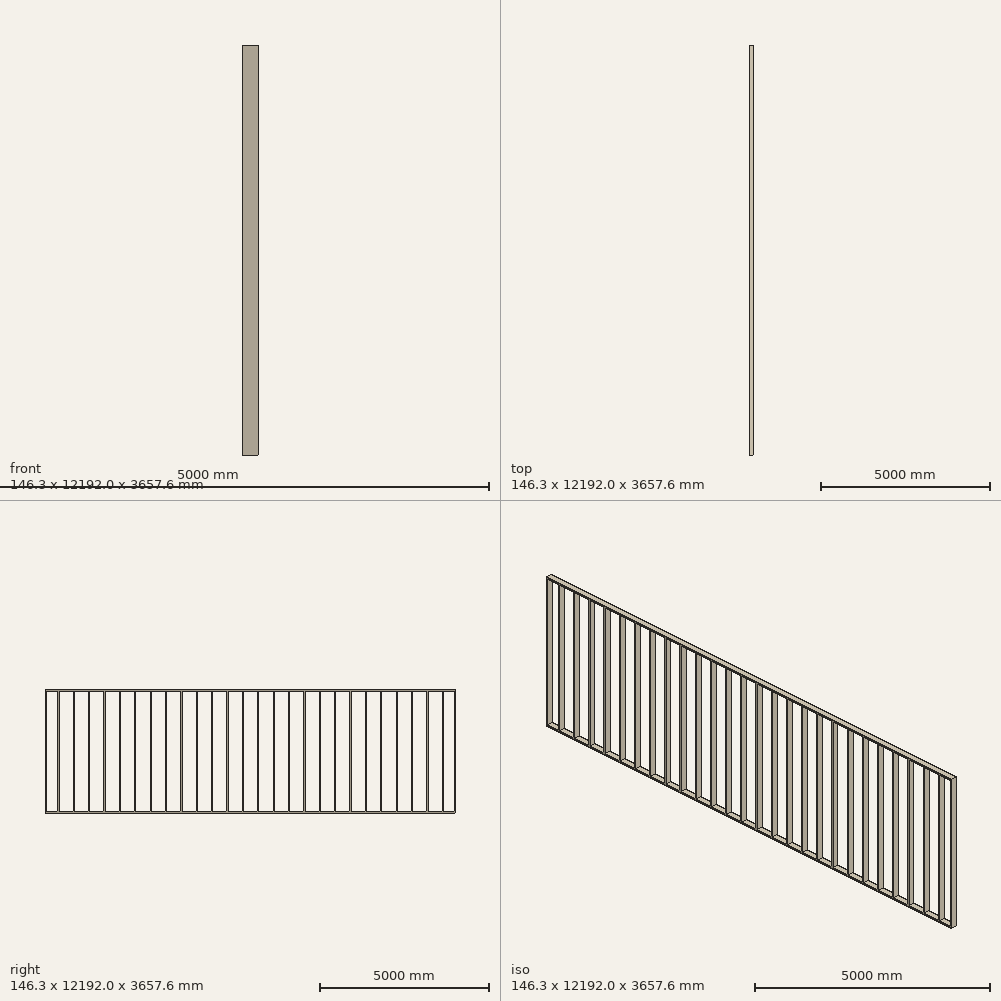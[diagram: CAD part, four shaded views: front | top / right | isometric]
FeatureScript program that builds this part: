
annotation { "Feature Type Name" : "Feature", "Feature Type Description" : "" }
export const myFeature = defineFeature(function(context is Context, id is Id, definition is map)
    precondition{}
    {
        {
            var Q0;
            Q0=qCreatedBy(makeId("Right.planeOp"),FACE);
            var sketch = newSketch(context, id + "F0", { "sketchPlane" : qUnion([Q0])});
            skLineSegment(sketch, "E0.bottom", {"start": v(0, 0) * mm, "end": v(12192, 0) * mm});
            skLineSegment(sketch, "E0.top", {"start": v(0, 3657.6) * mm, "end": v(12192, 3657.6) * mm});
            skLineSegment(sketch, "E0.left", {"start": v(0, 0) * mm, "end": v(0, 3657.6) * mm});
            skLineSegment(sketch, "E0.right", {"start": v(12192, 0) * mm, "end": v(12192, 3657.6) * mm});
            skLineSegment(sketch, "E1.0", {"start": v(38.1, 38.1) * mm, "end": v(38.1, 3619.5) * mm});
            skLineSegment(sketch, "E1.1", {"start": v(38.1, 38.1) * mm, "end": v(365.76, 38.1) * mm});
            skLineSegment(sketch, "E1.2", {"start": v(12153.9, 38.1) * mm, "end": v(12153.9, 3619.5) * mm});
            skLineSegment(sketch, "E1.3", {"start": v(38.1, 3619.5) * mm, "end": v(365.76, 3619.5) * mm});
            skLineSegment(sketch, "E2", {"start": v(365.76, 3619.5) * mm, "end": v(365.76, 38.1) * mm});
            skLineSegment(sketch, "E3", {"start": v(403.86, 3619.5) * mm, "end": v(403.86, 38.1) * mm});
            skLineSegment(sketch, "E4.trimOffspring", {"start": v(403.86, 3619.5) * mm, "end": v(822.96, 3619.5) * mm});
            skLineSegment(sketch, "E5.trimOffspring", {"start": v(403.86, 38.1) * mm, "end": v(822.96, 38.1) * mm});
            skLineSegment(sketch, "E6.1.0.0", {"start": v(822.96, 3619.5) * mm, "end": v(822.96, 38.1) * mm});
            skLineSegment(sketch, "E6.1.0.1", {"start": v(861.06, 3619.5) * mm, "end": v(861.06, 38.1) * mm});
            skLineSegment(sketch, "E6.2.0.0", {"start": v(1280.16, 3619.5) * mm, "end": v(1280.16, 38.1) * mm});
            skLineSegment(sketch, "E6.2.0.1", {"start": v(1318.26, 3619.5) * mm, "end": v(1318.26, 38.1) * mm});
            skLineSegment(sketch, "E6.3.0.0", {"start": v(1737.36, 3619.5) * mm, "end": v(1737.36, 38.1) * mm});
            skLineSegment(sketch, "E6.3.0.1", {"start": v(1775.46, 3619.5) * mm, "end": v(1775.46, 38.1) * mm});
            skLineSegment(sketch, "E6.4.0.0", {"start": v(2194.56, 3619.5) * mm, "end": v(2194.56, 38.1) * mm});
            skLineSegment(sketch, "E6.4.0.1", {"start": v(2232.66, 3619.5) * mm, "end": v(2232.66, 38.1) * mm});
            skLineSegment(sketch, "E6.5.0.0", {"start": v(2651.76, 3619.5) * mm, "end": v(2651.76, 38.1) * mm});
            skLineSegment(sketch, "E6.5.0.1", {"start": v(2689.86, 3619.5) * mm, "end": v(2689.86, 38.1) * mm});
            skLineSegment(sketch, "E6.6.0.0", {"start": v(3108.96, 3619.5) * mm, "end": v(3108.96, 38.1) * mm});
            skLineSegment(sketch, "E6.6.0.1", {"start": v(3147.06, 3619.5) * mm, "end": v(3147.06, 38.1) * mm});
            skLineSegment(sketch, "E6.7.0.0", {"start": v(3566.16, 3619.5) * mm, "end": v(3566.16, 38.1) * mm});
            skLineSegment(sketch, "E6.7.0.1", {"start": v(3604.26, 3619.5) * mm, "end": v(3604.26, 38.1) * mm});
            skLineSegment(sketch, "E6.8.0.0", {"start": v(4023.36, 3619.5) * mm, "end": v(4023.36, 38.1) * mm});
            skLineSegment(sketch, "E6.8.0.1", {"start": v(4061.46, 3619.5) * mm, "end": v(4061.46, 38.1) * mm});
            skLineSegment(sketch, "E6.9.0.0", {"start": v(4480.56, 3619.5) * mm, "end": v(4480.56, 38.1) * mm});
            skLineSegment(sketch, "E6.9.0.1", {"start": v(4518.66, 3619.5) * mm, "end": v(4518.66, 38.1) * mm});
            skLineSegment(sketch, "E6.10.0.0", {"start": v(4937.76, 3619.5) * mm, "end": v(4937.76, 38.1) * mm});
            skLineSegment(sketch, "E6.10.0.1", {"start": v(4975.86, 3619.5) * mm, "end": v(4975.86, 38.1) * mm});
            skLineSegment(sketch, "E6.11.0.0", {"start": v(5394.96, 3619.5) * mm, "end": v(5394.96, 38.1) * mm});
            skLineSegment(sketch, "E6.11.0.1", {"start": v(5433.06, 3619.5) * mm, "end": v(5433.06, 38.1) * mm});
            skLineSegment(sketch, "E6.12.0.0", {"start": v(5852.16, 3619.5) * mm, "end": v(5852.16, 38.1) * mm});
            skLineSegment(sketch, "E6.12.0.1", {"start": v(5890.26, 3619.5) * mm, "end": v(5890.26, 38.1) * mm});
            skLineSegment(sketch, "E6.13.0.0", {"start": v(6309.36, 3619.5) * mm, "end": v(6309.36, 38.1) * mm});
            skLineSegment(sketch, "E6.13.0.1", {"start": v(6347.46, 3619.5) * mm, "end": v(6347.46, 38.1) * mm});
            skLineSegment(sketch, "E6.14.0.0", {"start": v(6766.56, 3619.5) * mm, "end": v(6766.56, 38.1) * mm});
            skLineSegment(sketch, "E6.14.0.1", {"start": v(6804.66, 3619.5) * mm, "end": v(6804.66, 38.1) * mm});
            skLineSegment(sketch, "E6.15.0.0", {"start": v(7223.76, 3619.5) * mm, "end": v(7223.76, 38.1) * mm});
            skLineSegment(sketch, "E6.15.0.1", {"start": v(7261.86, 3619.5) * mm, "end": v(7261.86, 38.1) * mm});
            skLineSegment(sketch, "E6.16.0.0", {"start": v(7680.96, 3619.5) * mm, "end": v(7680.96, 38.1) * mm});
            skLineSegment(sketch, "E6.16.0.1", {"start": v(7719.06, 3619.5) * mm, "end": v(7719.06, 38.1) * mm});
            skLineSegment(sketch, "E6.17.0.0", {"start": v(8138.16, 3619.5) * mm, "end": v(8138.16, 38.1) * mm});
            skLineSegment(sketch, "E6.17.0.1", {"start": v(8176.26, 3619.5) * mm, "end": v(8176.26, 38.1) * mm});
            skLineSegment(sketch, "E6.18.0.0", {"start": v(8595.36, 3619.5) * mm, "end": v(8595.36, 38.1) * mm});
            skLineSegment(sketch, "E6.18.0.1", {"start": v(8633.46, 3619.5) * mm, "end": v(8633.46, 38.1) * mm});
            skLineSegment(sketch, "E6.19.0.0", {"start": v(9052.56, 3619.5) * mm, "end": v(9052.56, 38.1) * mm});
            skLineSegment(sketch, "E6.19.0.1", {"start": v(9090.66, 3619.5) * mm, "end": v(9090.66, 38.1) * mm});
            skLineSegment(sketch, "E6.20.0.0", {"start": v(9509.76, 3619.5) * mm, "end": v(9509.76, 38.1) * mm});
            skLineSegment(sketch, "E6.20.0.1", {"start": v(9547.86, 3619.5) * mm, "end": v(9547.86, 38.1) * mm});
            skLineSegment(sketch, "E6.21.0.0", {"start": v(9966.96, 3619.5) * mm, "end": v(9966.96, 38.1) * mm});
            skLineSegment(sketch, "E6.21.0.1", {"start": v(10005.06, 3619.5) * mm, "end": v(10005.06, 38.1) * mm});
            skLineSegment(sketch, "E6.22.0.0", {"start": v(10424.16, 3619.5) * mm, "end": v(10424.16, 38.1) * mm});
            skLineSegment(sketch, "E6.22.0.1", {"start": v(10462.26, 3619.5) * mm, "end": v(10462.26, 38.1) * mm});
            skLineSegment(sketch, "E6.23.0.0", {"start": v(10881.36, 3619.5) * mm, "end": v(10881.36, 38.1) * mm});
            skLineSegment(sketch, "E6.23.0.1", {"start": v(10919.46, 3619.5) * mm, "end": v(10919.46, 38.1) * mm});
            skLineSegment(sketch, "E6.24.0.0", {"start": v(11338.56, 3619.5) * mm, "end": v(11338.56, 38.1) * mm});
            skLineSegment(sketch, "E6.24.0.1", {"start": v(11376.66, 3619.5) * mm, "end": v(11376.66, 38.1) * mm});
            skLineSegment(sketch, "E6.25.0.0", {"start": v(11795.76, 3619.5) * mm, "end": v(11795.76, 38.1) * mm});
            skLineSegment(sketch, "E6.25.0.1", {"start": v(11833.86, 3619.5) * mm, "end": v(11833.86, 38.1) * mm});
            skLineSegment(sketch, "E6.direction1", {"start": v(403.86, 38.1) * mm, "end": v(822.96, 38.1) * mm, "construction": true});
            skLineSegment(sketch, "E7.trimOffspring", {"start": v(861.06, 3619.5) * mm, "end": v(1280.16, 3619.5) * mm});
            skLineSegment(sketch, "E8.trimOffspring", {"start": v(1318.26, 3619.5) * mm, "end": v(1737.36, 3619.5) * mm});
            skLineSegment(sketch, "E9.trimOffspring", {"start": v(1775.46, 3619.5) * mm, "end": v(2194.56, 3619.5) * mm});
            skLineSegment(sketch, "E10.trimOffspring", {"start": v(2232.66, 3619.5) * mm, "end": v(2651.76, 3619.5) * mm});
            skLineSegment(sketch, "E11.trimOffspring", {"start": v(2689.86, 3619.5) * mm, "end": v(3108.96, 3619.5) * mm});
            skLineSegment(sketch, "E12.trimOffspring", {"start": v(3147.06, 3619.5) * mm, "end": v(3566.16, 3619.5) * mm});
            skLineSegment(sketch, "E13.trimOffspring", {"start": v(3604.26, 3619.5) * mm, "end": v(4023.36, 3619.5) * mm});
            skLineSegment(sketch, "E14.trimOffspring", {"start": v(4061.46, 3619.5) * mm, "end": v(4480.56, 3619.5) * mm});
            skLineSegment(sketch, "E15.trimOffspring", {"start": v(4518.66, 3619.5) * mm, "end": v(4937.76, 3619.5) * mm});
            skLineSegment(sketch, "E16.trimOffspring", {"start": v(4975.86, 3619.5) * mm, "end": v(5394.96, 3619.5) * mm});
            skLineSegment(sketch, "E17.trimOffspring", {"start": v(5433.06, 3619.5) * mm, "end": v(5852.16, 3619.5) * mm});
            skLineSegment(sketch, "E18.trimOffspring", {"start": v(5890.26, 3619.5) * mm, "end": v(6309.36, 3619.5) * mm});
            skLineSegment(sketch, "E19.trimOffspring", {"start": v(6347.46, 3619.5) * mm, "end": v(6766.56, 3619.5) * mm});
            skLineSegment(sketch, "E20.trimOffspring", {"start": v(6804.66, 3619.5) * mm, "end": v(7223.76, 3619.5) * mm});
            skLineSegment(sketch, "E21.trimOffspring", {"start": v(7261.86, 3619.5) * mm, "end": v(7680.96, 3619.5) * mm});
            skLineSegment(sketch, "E22.trimOffspring", {"start": v(7719.06, 3619.5) * mm, "end": v(8138.16, 3619.5) * mm});
            skLineSegment(sketch, "E23.trimOffspring", {"start": v(8176.26, 3619.5) * mm, "end": v(8595.36, 3619.5) * mm});
            skLineSegment(sketch, "E24.trimOffspring", {"start": v(8633.46, 3619.5) * mm, "end": v(9052.56, 3619.5) * mm});
            skLineSegment(sketch, "E25.trimOffspring", {"start": v(9090.66, 3619.5) * mm, "end": v(9509.76, 3619.5) * mm});
            skLineSegment(sketch, "E26.trimOffspring", {"start": v(9547.86, 3619.5) * mm, "end": v(9966.96, 3619.5) * mm});
            skLineSegment(sketch, "E27.trimOffspring", {"start": v(10005.06, 3619.5) * mm, "end": v(10424.16, 3619.5) * mm});
            skLineSegment(sketch, "E28.trimOffspring", {"start": v(10462.26, 3619.5) * mm, "end": v(10881.36, 3619.5) * mm});
            skLineSegment(sketch, "E29.trimOffspring", {"start": v(10919.46, 3619.5) * mm, "end": v(11338.56, 3619.5) * mm});
            skLineSegment(sketch, "E30.trimOffspring", {"start": v(11376.66, 3619.5) * mm, "end": v(11795.76, 3619.5) * mm});
            skLineSegment(sketch, "E31.trimOffspring", {"start": v(11833.86, 3619.5) * mm, "end": v(12153.9, 3619.5) * mm});
            skLineSegment(sketch, "E32.trimOffspring", {"start": v(11833.86, 38.1) * mm, "end": v(12153.9, 38.1) * mm});
            skLineSegment(sketch, "E33.trimOffspring", {"start": v(11376.66, 38.1) * mm, "end": v(11795.76, 38.1) * mm});
            skLineSegment(sketch, "E34.trimOffspring", {"start": v(10919.46, 38.1) * mm, "end": v(11338.56, 38.1) * mm});
            skLineSegment(sketch, "E35.trimOffspring", {"start": v(10462.26, 38.1) * mm, "end": v(10881.36, 38.1) * mm});
            skLineSegment(sketch, "E36.trimOffspring", {"start": v(10005.06, 38.1) * mm, "end": v(10424.16, 38.1) * mm});
            skLineSegment(sketch, "E37.trimOffspring", {"start": v(9547.86, 38.1) * mm, "end": v(9966.96, 38.1) * mm});
            skLineSegment(sketch, "E38.trimOffspring", {"start": v(9090.66, 38.1) * mm, "end": v(9509.76, 38.1) * mm});
            skLineSegment(sketch, "E39.trimOffspring", {"start": v(8633.46, 38.1) * mm, "end": v(9052.56, 38.1) * mm});
            skLineSegment(sketch, "E40.trimOffspring", {"start": v(8176.26, 38.1) * mm, "end": v(8595.36, 38.1) * mm});
            skLineSegment(sketch, "E41.trimOffspring", {"start": v(7719.06, 38.1) * mm, "end": v(8138.16, 38.1) * mm});
            skLineSegment(sketch, "E42.trimOffspring", {"start": v(7261.86, 38.1) * mm, "end": v(7680.96, 38.1) * mm});
            skLineSegment(sketch, "E43.trimOffspring", {"start": v(6804.66, 38.1) * mm, "end": v(7223.76, 38.1) * mm});
            skLineSegment(sketch, "E44.trimOffspring", {"start": v(6347.46, 38.1) * mm, "end": v(6766.56, 38.1) * mm});
            skLineSegment(sketch, "E45.trimOffspring", {"start": v(5890.26, 38.1) * mm, "end": v(6309.36, 38.1) * mm});
            skLineSegment(sketch, "E46.trimOffspring", {"start": v(5433.06, 38.1) * mm, "end": v(5852.16, 38.1) * mm});
            skLineSegment(sketch, "E47.trimOffspring", {"start": v(4975.86, 38.1) * mm, "end": v(5394.96, 38.1) * mm});
            skLineSegment(sketch, "E48.trimOffspring", {"start": v(4518.66, 38.1) * mm, "end": v(4937.76, 38.1) * mm});
            skLineSegment(sketch, "E49.trimOffspring", {"start": v(4061.46, 38.1) * mm, "end": v(4480.56, 38.1) * mm});
            skLineSegment(sketch, "E50.trimOffspring", {"start": v(3604.26, 38.1) * mm, "end": v(4023.36, 38.1) * mm});
            skLineSegment(sketch, "E51.trimOffspring", {"start": v(3147.06, 38.1) * mm, "end": v(3566.16, 38.1) * mm});
            skLineSegment(sketch, "E52.trimOffspring", {"start": v(2689.86, 38.1) * mm, "end": v(3108.96, 38.1) * mm});
            skLineSegment(sketch, "E53.trimOffspring", {"start": v(2232.66, 38.1) * mm, "end": v(2651.76, 38.1) * mm});
            skLineSegment(sketch, "E54.trimOffspring", {"start": v(1775.46, 38.1) * mm, "end": v(2194.56, 38.1) * mm});
            skLineSegment(sketch, "E55.trimOffspring", {"start": v(1318.26, 38.1) * mm, "end": v(1737.36, 38.1) * mm});
            skLineSegment(sketch, "E56.trimOffspring", {"start": v(861.06, 38.1) * mm, "end": v(1280.16, 38.1) * mm});
            skSolve(sketch);
        }
        {
            var Q0;
            Q0 = qSketchRegion(id + "F0", true);
            extrude(context, id + "F1", {"entities" : qUnion([Q0]), "depth" : 146.3 * mm, "offsetDistance" : 30.48 * mm});
        }
    });
